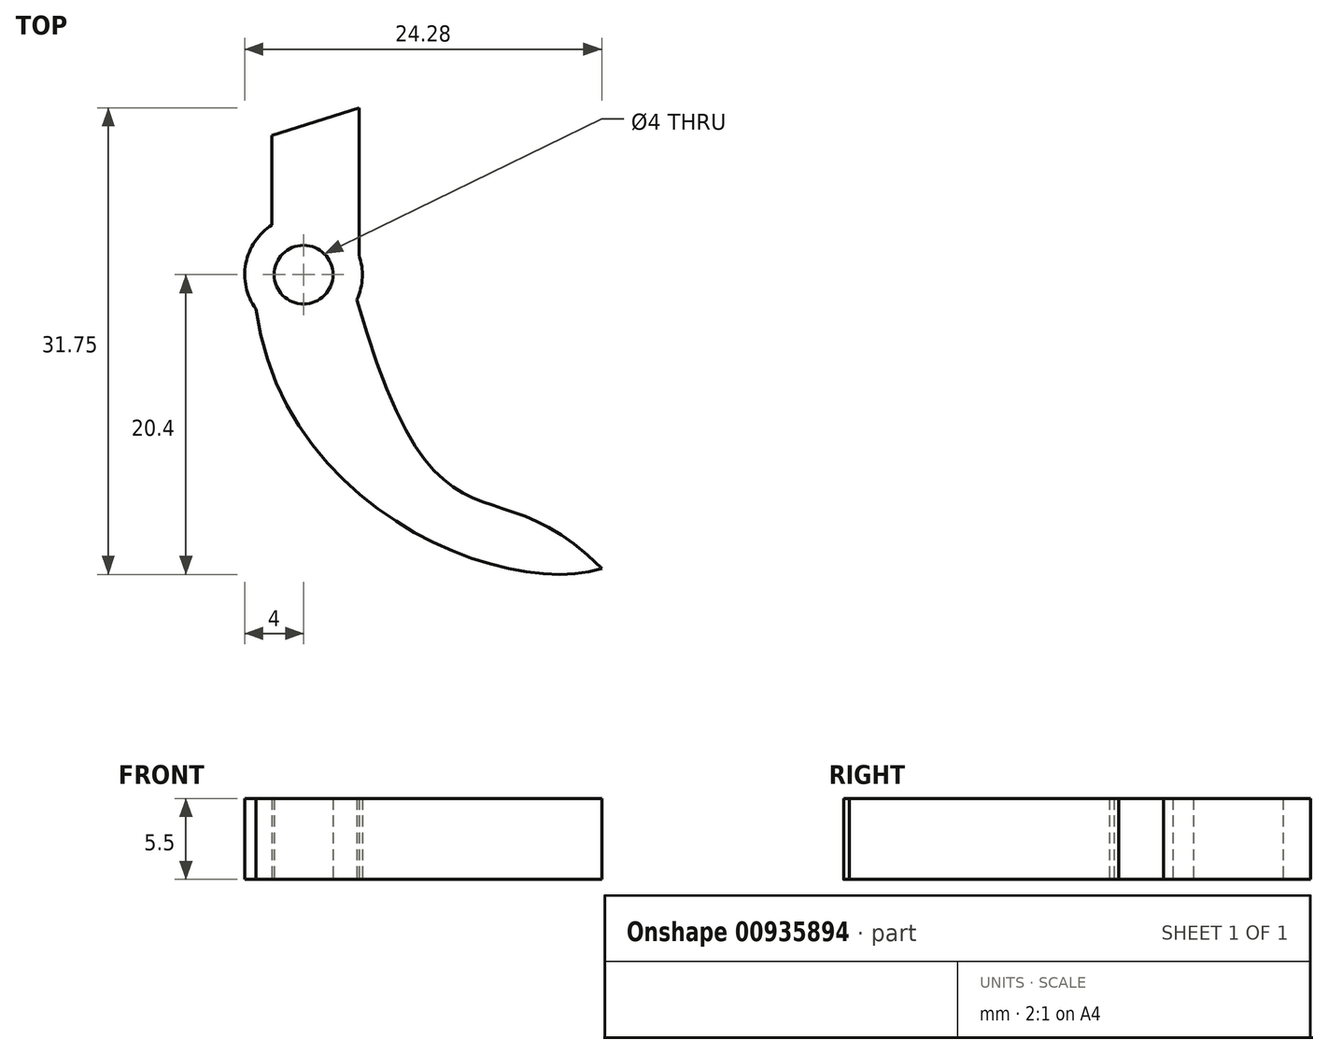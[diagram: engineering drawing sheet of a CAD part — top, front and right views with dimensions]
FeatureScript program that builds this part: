
annotation { "Feature Type Name" : "Feature", "Feature Type Description" : "" }
export const myFeature = defineFeature(function(context is Context, id is Id, definition is map)
    precondition{}
    {
        {
            var Q0;
            Q0=qCreatedBy(makeId("Top.planeOp"),FACE);
            var sketch = newSketch(context, id + "F0", { "sketchPlane" : qUnion([Q0])});
            skCircle(sketch, "E0", {"center": v(0, 0) * mm, "radius": 2 * mm});
            skCircle(sketch, "E1", {"center": v(0, 0) * mm, "radius": 4 * mm});
            skFitSpline(sketch, "E2", {"points": [v(3.62, -1.7) * mm, v(20.28, -20) * mm], "startDerivative": vector(16.08, -56.49) * mm, "endDerivative": vector(22.54, -23.18) * mm});
            skFitSpline(sketch, "E3", {"points": [v(20.28, -20) * mm, v(-3.25, -2.33) * mm], "startDerivative": vector(-18.7, -6.11) * mm, "endDerivative": vector(-5.84, 41.9) * mm});
            skLineSegment(sketch, "E4", {"start": v(3.77, 1.35) * mm, "end": v(3.77, 11.35) * mm});
            skLineSegment(sketch, "E5", {"start": v(3.77, 11.35) * mm, "end": v(-2.14, 9.48) * mm});
            skLineSegment(sketch, "E6", {"start": v(-2.14, 9.48) * mm, "end": v(-2.14, 3.38) * mm});
            skSolve(sketch);
        }
        {
            var Q0;
            {var subQ0=sQuery(id+"F0.wireOp",EDGE,"E2");Q0=makeQuery(id+"F0.imprint","IMPRINT",FACE,{"disambiguationData":[TD([[makeQuery(id+"F0.imprint","IMPRINT",EDGE,{"derivedFrom":subQ0}),-1.0]])]});}
            var Q1;
            Q1=makeQuery(id+"F0.imprint","IMPRINT",FACE,{"disambiguationData":[TD([[makeQuery(id+"F0.imprint","IMPRINT",EDGE,{"derivedFrom":sQuery(id+"F0.wireOp",EDGE,"E0")}),-1.0]])]});
            var Q2;
            {var subQ0=sQuery(id+"F0.wireOp",EDGE,"E4");Q2=makeQuery(id+"F0.imprint","IMPRINT",FACE,{"disambiguationData":[TD([[makeQuery(id+"F0.imprint","IMPRINT",EDGE,{"derivedFrom":subQ0}),1.0]])]});}
            extrude(context, id + "F1", {"entities" : qUnion([Q0, Q1, Q2]), "depth" : 5.5 * mm, "offsetDistance" : 25 * mm});
        }
    });
